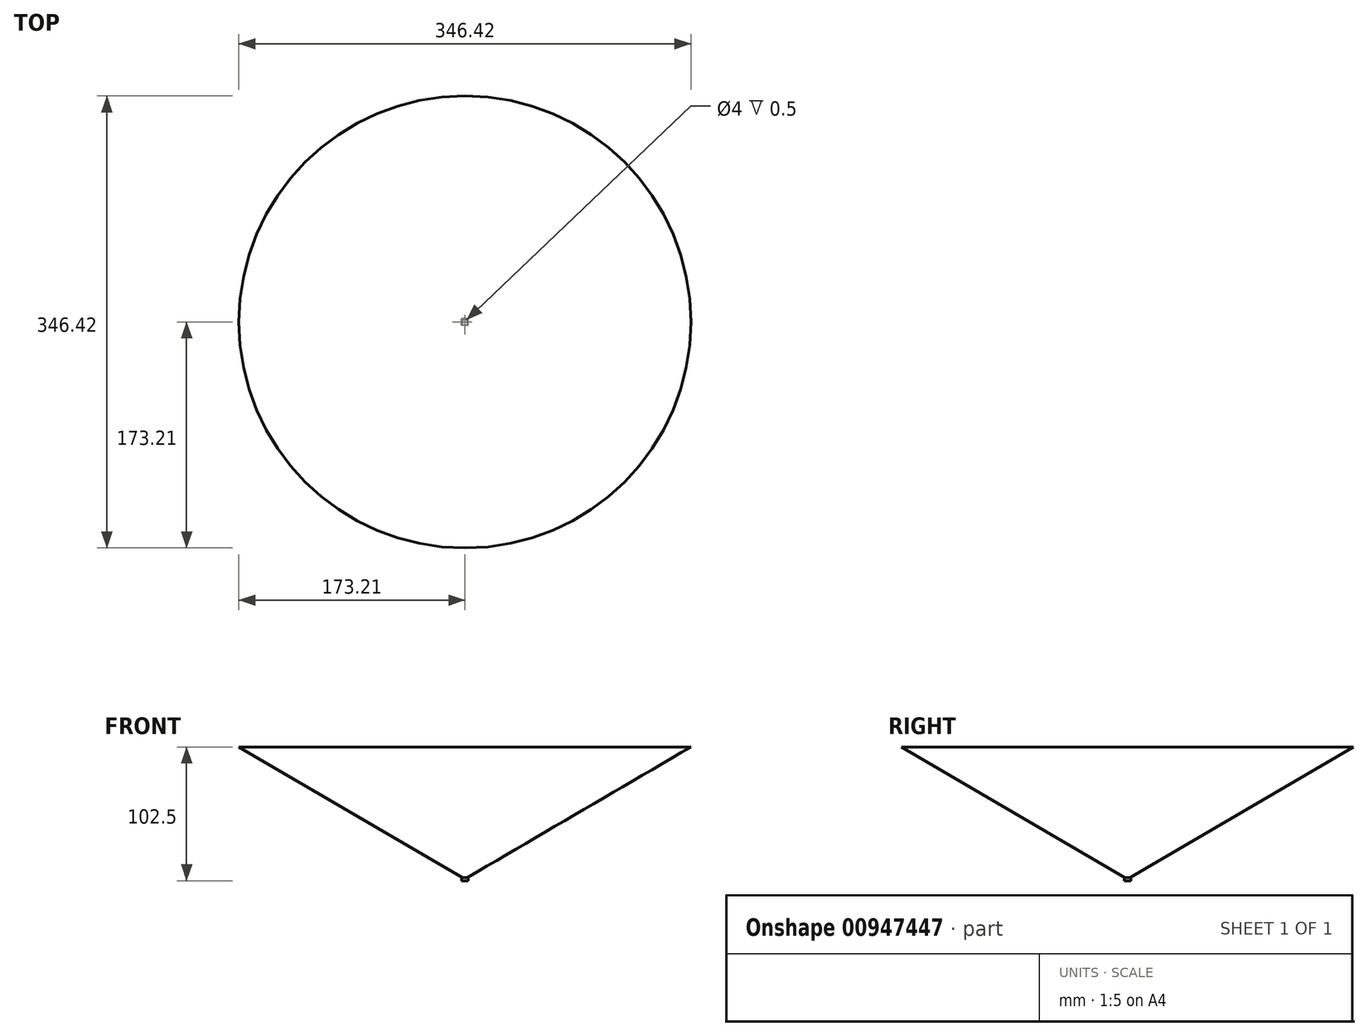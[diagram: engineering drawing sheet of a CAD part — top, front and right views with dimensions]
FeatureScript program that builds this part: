
annotation { "Feature Type Name" : "Feature", "Feature Type Description" : "" }
export const myFeature = defineFeature(function(context is Context, id is Id, definition is map)
    precondition{}
    {
        {
            var Q0;
            Q0=qCreatedBy(makeId("Top.planeOp"),FACE);
            var sketch = newSketch(context, id + "F0", { "sketchPlane" : qUnion([Q0])});
            skLineSegment(sketch, "E0.bottom", {"start": v(2.5, -2.5) * mm, "end": v(-2.5, -2.5) * mm});
            skLineSegment(sketch, "E0.top", {"start": v(2.5, 2.5) * mm, "end": v(-2.5, 2.5) * mm});
            skLineSegment(sketch, "E0.left", {"start": v(2.5, -2.5) * mm, "end": v(2.5, 2.5) * mm});
            skLineSegment(sketch, "E0.right", {"start": v(-2.5, -2.5) * mm, "end": v(-2.5, 2.5) * mm});
            skPoint(sketch, "E0.middle", {"position": v(0, 0) * mm});
            skSolve(sketch);
        }
        {
            var Q0;
            Q0=makeQuery(id+"F0.imprint","IMPRINT",FACE,{"disambiguationData":[TD([[makeQuery(id+"F0.imprint","IMPRINT",EDGE,{"derivedFrom":sQuery(id+"F0.wireOp",EDGE,"E0.bottom")}),-1.0]])]});
            extrude(context, id + "F1", {"entities" : qUnion([Q0]), "depth" : 2.5 * mm, "offsetDistance" : 25 * mm});
        }
        {
            var Q0;
            Q0=makeQuery(id+"F1.opExtrude","CAP_FACE",FACE,{"disambiguationData":[OSD([sQuery(id+"F0.wireOp",EDGE,"E0.bottom"),sQuery(id+"F0.wireOp",EDGE,"E0.top"),sQuery(id+"F0.wireOp",EDGE,"E0.left"),sQuery(id+"F0.wireOp",EDGE,"E0.right")])],"isStart":false});
            var sketch = newSketch(context, id + "F2", { "sketchPlane" : qUnion([Q0])});
            skCircle(sketch, "E1", {"center": v(0, 0) * mm, "radius": 2 * mm});
            skSolve(sketch);
        }
        {
            var Q0;
            Q0=makeQuery(id+"F2.imprint","IMPRINT",FACE,{"disambiguationData":[TD([[makeQuery(id+"F2.imprint","IMPRINT",EDGE,{"derivedFrom":sQuery(id+"F2.wireOp",EDGE,"E1")}),1.0]])]});
            extrude(context, id + "F3", {"entities" : qUnion([Q0]), "operationType" : NewBodyOperationType.REMOVE, "oppositeDirection" : true, "depth" : 0.5 * mm, "offsetDistance" : 25 * mm});
        }
        {
            var Q0;
            Q0=qCreatedBy(makeId("Right.planeOp"),FACE);
            var sketch = newSketch(context, id + "F4", { "sketchPlane" : qUnion([Q0])});
            skLineSegment(sketch, "E2.0", {"start": v(-2.5, 2.5) * mm, "end": v(2.5, 2.5) * mm, "construction": true});
            skPoint(sketch, "E3", {"position": v(-2, 2.5) * mm});
            skPoint(sketch, "E4", {"position": v(2, 2.5) * mm});
            skLineSegment(sketch, "E5", {"start": v(-2, 2.5) * mm, "end": v(-173.2, 102.5) * mm});
            skLineSegment(sketch, "E6", {"start": v(-173.2, 102.5) * mm, "end": v(0, 102.5) * mm});
            skPoint(sketch, "E7", {"position": v(0, 2.5) * mm});
            skLineSegment(sketch, "E8", {"start": v(0, 2.5) * mm, "end": v(0, 7.3) * mm, "construction": true});
            skLineSegment(sketch, "E9", {"start": v(0, 2.5) * mm, "end": v(-2.67, 4.04) * mm, "construction": true});
            skLineSegment(sketch, "E10", {"start": v(-2, 2.5) * mm, "end": v(0, 2.5) * mm});
            skLineSegment(sketch, "E11", {"start": v(0, 102.5) * mm, "end": v(0, 2.5) * mm});
            skSolve(sketch);
        }
        {
            var Q0;
            Q0=makeQuery(id+"F4.imprint","IMPRINT",FACE,{"disambiguationData":[TD([[makeQuery(id+"F4.imprint","IMPRINT",EDGE,{"derivedFrom":sQuery(id+"F4.wireOp",EDGE,"E5")}),-1.0]])]});
            var Q1;
            Q1=sQuery(id+"F4.wireOp",EDGE,"E11");
            revolve(context, id + "F5", {"surfaceOperationType" : NewSurfaceOperationType.NEW, "entities" : qUnion([Q0]), "axis" : qUnion([Q1]), "revolveType" : RevolveType.FULL});
        }
    });
